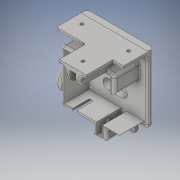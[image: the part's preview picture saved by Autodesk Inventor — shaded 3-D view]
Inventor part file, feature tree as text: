
AUTODESK INVENTOR PART (.ipt)
format: ipt  version: 2016 (Build 200138000, 138)  size: 1,051,136 bytes
history: native  units: in
note: dims shown in document units (in); Inventor stores cm internally (conversion verified against a paired STEP export)
features: sketch x18, plane x4, other x3
ambient origin geometry x8: Origin, YZ Plane, XZ Plane, XY Plane, X Axis, Y Axis, Z Axis, Center Point
bodies: Solid1 (feature_tree)
feature tree (25):
  other  "ankle_holder.ipt"
  other  "Solid1::ankle_holder.ipt"
  other  "TaggingFeature1"
  sketch  "Sketch1"  dims[d0=0.3937in]
  sketch  "Sketch12"
  sketch  "Sketch14"
  sketch  "Sketch17"
  sketch  "Sketch18"
  sketch  "Sketch22"
  sketch  "Sketch24"
  sketch  "Sketch30"
  sketch  "Sketch32"
  sketch  "Sketch33"
  sketch  "Sketch35"
  sketch  "Sketch36"
  sketch  "Sketch37"
  sketch  "Sketch38"
  sketch  "Sketch40"
  sketch  "Sketch41"
  sketch  "Sketch42"
  sketch  "Sketch43"
  plane  "Work Plane1"
  plane  "Work Plane4"
  plane  "Work Plane5"
  plane  "Work Plane6"
